annotation { "Feature Type Name" : "Feature", "Feature Type Description" : "" }
export const myFeature = defineFeature(function(context is Context, id is Id, definition is map)
    precondition{}
    {
        {
            var Q0;
            Q0=qCreatedBy(makeId("Top.planeOp"),FACE);
            var sketch = newSketch(context, id + "F0", { "sketchPlane" : qUnion([Q0])});
            skLineSegment(sketch, "E0.top", {"start": v(0, -101.6) * mm, "end": v(203.2, -101.6) * mm});
            skLineSegment(sketch, "E0.left", {"start": v(0, 0) * mm, "end": v(0, -101.6) * mm});
            skLineSegment(sketch, "E0.right", {"start": v(203.2, 0) * mm, "end": v(203.2, -101.6) * mm});
            skLineSegment(sketch, "E1.left", {"start": v(3.18, -3.17) * mm, "end": v(3.18, -98.43) * mm});
            skLineSegment(sketch, "E1.right", {"start": v(200.03, -3.17) * mm, "end": v(200.03, -98.43) * mm});
            skLineSegment(sketch, "E2", {"start": v(3.17, -3.17) * mm, "end": v(33.34, -3.17) * mm});
            skLineSegment(sketch, "E3", {"start": v(203.2, 0) * mm, "end": v(0, 0) * mm});
            skLineSegment(sketch, "E4", {"start": v(3.18, -98.43) * mm, "end": v(200.03, -98.43) * mm});
            skLineSegment(sketch, "E5.top", {"start": v(18.18, -98.43) * mm, "end": v(18.18, -98.43) * mm});
            skLineSegment(sketch, "E6", {"start": v(33.34, -98.43) * mm, "end": v(33.34, -3.17) * mm});
            skLineSegment(sketch, "E7", {"start": v(36.51, -3.17) * mm, "end": v(36.51, -3.17) * mm});
            skLineSegment(sketch, "E8", {"start": v(36.51, -3.17) * mm, "end": v(36.51, -98.43) * mm});
            skLineSegment(sketch, "E9", {"start": v(36.51, -3.17) * mm, "end": v(66.68, -3.17) * mm});
            skLineSegment(sketch, "E10", {"start": v(66.68, -98.42) * mm, "end": v(66.68, -3.17) * mm});
            skLineSegment(sketch, "E11", {"start": v(69.85, -3.17) * mm, "end": v(69.85, -98.42) * mm});
            skLineSegment(sketch, "E12", {"start": v(69.85, -3.17) * mm, "end": v(100.01, -3.17) * mm});
            skLineSegment(sketch, "E13", {"start": v(100.01, -3.17) * mm, "end": v(100.01, -98.42) * mm});
            skLineSegment(sketch, "E14", {"start": v(103.19, -3.17) * mm, "end": v(103.19, -98.42) * mm});
            skLineSegment(sketch, "E15", {"start": v(117.07, -3.17) * mm, "end": v(133.35, -3.17) * mm});
            skLineSegment(sketch, "E16", {"start": v(133.35, -3.17) * mm, "end": v(133.35, -98.42) * mm});
            skLineSegment(sketch, "E17", {"start": v(103.19, -3.17) * mm, "end": v(117.07, -3.17) * mm});
            skLineSegment(sketch, "E18", {"start": v(136.52, -3.17) * mm, "end": v(136.53, -98.42) * mm});
            skLineSegment(sketch, "E19", {"start": v(133.35, -3.17) * mm, "end": v(133.35, -3.17) * mm});
            skLineSegment(sketch, "E20", {"start": v(136.52, -3.17) * mm, "end": v(166.69, -3.17) * mm});
            skLineSegment(sketch, "E21", {"start": v(166.69, -3.17) * mm, "end": v(166.69, -98.42) * mm});
            skLineSegment(sketch, "E22", {"start": v(169.86, -3.17) * mm, "end": v(169.86, -98.42) * mm});
            skLineSegment(sketch, "E23", {"start": v(169.86, -3.17) * mm, "end": v(200.03, -3.17) * mm});
            skSolve(sketch);
        }
        {
            var Q0;
            Q0=makeQuery(id+"F0.imprint","IMPRINT",FACE,{"disambiguationData":[TD([[makeQuery(id+"F0.imprint","IMPRINT",EDGE,{"derivedFrom":sQuery(id+"F0.wireOp",EDGE,"E0.top")}),1.0]])]});
            var Q1;
            Q1=makeQuery(id+"F0.imprint","IMPRINT",FACE,{"disambiguationData":[TD([[makeQuery(id+"F0.imprint","IMPRINT",EDGE,{"derivedFrom":sQuery(id+"F0.wireOp",EDGE,"E5.bottom")}),-1.0]])]});
            var Q2;
            {var subQ0=sQuery(id+"F0.wireOp",EDGE,"646c8ae3-f2b2-429d-8022-bc64b3b6f105.1.0.0");Q2=makeQuery(id+"F0.imprint","IMPRINT",FACE,{"disambiguationData":[TD([[makeQuery(id+"F0.imprint","IMPRINT",EDGE,{"derivedFrom":subQ0}),1.0]])]});}
            var Q3;
            {var subQ0=sQuery(id+"F0.wireOp",EDGE,"646c8ae3-f2b2-429d-8022-bc64b3b6f105.2.0.0");Q3=makeQuery(id+"F0.imprint","IMPRINT",FACE,{"disambiguationData":[TD([[makeQuery(id+"F0.imprint","IMPRINT",EDGE,{"derivedFrom":subQ0}),1.0]])]});}
            var Q4;
            {var subQ0=sQuery(id+"F0.wireOp",EDGE,"646c8ae3-f2b2-429d-8022-bc64b3b6f105.3.0.0");Q4=makeQuery(id+"F0.imprint","IMPRINT",FACE,{"disambiguationData":[TD([[makeQuery(id+"F0.imprint","IMPRINT",EDGE,{"derivedFrom":subQ0}),1.0]])]});}
            var Q5;
            {var subQ0=sQuery(id+"F0.wireOp",EDGE,"646c8ae3-f2b2-429d-8022-bc64b3b6f105.4.0.0");Q5=makeQuery(id+"F0.imprint","IMPRINT",FACE,{"disambiguationData":[TD([[makeQuery(id+"F0.imprint","IMPRINT",EDGE,{"derivedFrom":subQ0}),1.0]])]});}
            var Q6;
            {var subQ0=sQuery(id+"F0.wireOp",EDGE,"646c8ae3-f2b2-429d-8022-bc64b3b6f105.5.0.0");Q6=makeQuery(id+"F0.imprint","IMPRINT",FACE,{"disambiguationData":[TD([[makeQuery(id+"F0.imprint","IMPRINT",EDGE,{"derivedFrom":subQ0}),1.0]])]});}
            var Q7;
            {var subQ0=sQuery(id+"F0.wireOp",EDGE,"646c8ae3-f2b2-429d-8022-bc64b3b6f105.6.0.0");Q7=makeQuery(id+"F0.imprint","IMPRINT",FACE,{"disambiguationData":[TD([[makeQuery(id+"F0.imprint","IMPRINT",EDGE,{"derivedFrom":subQ0}),1.0]])]});}
            var Q8;
            {var subQ0=sQuery(id+"F0.wireOp",EDGE,"646c8ae3-f2b2-429d-8022-bc64b3b6f105.7.0.0");Q8=makeQuery(id+"F0.imprint","IMPRINT",FACE,{"disambiguationData":[TD([[makeQuery(id+"F0.imprint","IMPRINT",EDGE,{"derivedFrom":subQ0}),1.0]])]});}
            var Q9;
            {var subQ0=sQuery(id+"F0.wireOp",EDGE,"646c8ae3-f2b2-429d-8022-bc64b3b6f105.8.0.0");Q9=makeQuery(id+"F0.imprint","IMPRINT",FACE,{"disambiguationData":[TD([[makeQuery(id+"F0.imprint","IMPRINT",EDGE,{"derivedFrom":subQ0}),1.0]])]});}
            var Q10;
            {var subQ0=sQuery(id+"F0.wireOp",EDGE,"646c8ae3-f2b2-429d-8022-bc64b3b6f105.9.0.0");Q10=makeQuery(id+"F0.imprint","IMPRINT",FACE,{"disambiguationData":[TD([[makeQuery(id+"F0.imprint","IMPRINT",EDGE,{"derivedFrom":subQ0}),1.0]])]});}
            extrude(context, id + "F1", {"entities" : qUnion([Q0, Q1, Q2, Q3, Q4, Q5, Q6, Q7, Q8, Q9, Q10]), "depth" : 47.62 * mm, "offsetDistance" : 25.4 * mm});
        }
        {
            var Q0;
            Q0=makeQuery(id+"FWKmPxKbktaoT75_1.boolean.opBoolean","MERGE",FACE,{"derivedFrom":[makeQuery(id+"F1.opExtrude","SWEPT_FACE",FACE,{"disambiguationData":[OSD([sQuery(id+"F0.wireOp",EDGE,"E0.top")])]}),makeQuery(id+"FWKmPxKbktaoT75_1.opExtrude","SWEPT_FACE",FACE,{"disambiguationData":[OSD([sQuery(id+"FPa2vzEjn9xWxvl_1.wireOp",EDGE,"pVME8pcI-fUVT-DpI0-aKQs-MaaHCtd98V99.bottom")])]})]});
            var sketch = newSketch(context, id + "F2", { "sketchPlane" : qUnion([Q0])});
            skText(sketch, "E24", { "text": "Black Heat Shrink", "fontName": "OpenSans-Regular.ttf"});
            const initialGuessF2  = {"E24": [0.00394, 0.01524, 1, 0, 0.01715]};
            skSetInitialGuess(sketch, initialGuessF2);
            skSolve(sketch);
        }
        {
            var Q0;
            Q0=qSketchRegion(id+"F2",true);
            extrude(context, id + "F3", {"entities" : qUnion([Q0]), "operationType" : NewBodyOperationType.REMOVE, "oppositeDirection" : true, "depth" : 0.25 * mm, "offsetDistance" : 25.4 * mm});
        }
        {
            var Q0;
            Q0=makeQuery(id+"F1.opExtrude","CAP_FACE",FACE,{"disambiguationData":[OSD([sQuery(id+"F0.wireOp",EDGE,"E0.top"),sQuery(id+"F0.wireOp",EDGE,"E0.left"),sQuery(id+"F0.wireOp",EDGE,"E0.right"),sQuery(id+"F0.wireOp",EDGE,"E1.left"),sQuery(id+"F0.wireOp",EDGE,"E1.right"),sQuery(id+"F0.wireOp",EDGE,"E2"),sQuery(id+"F0.wireOp",EDGE,"E3"),sQuery(id+"F0.wireOp",EDGE,"E4"),sQuery(id+"F0.wireOp",EDGE,"E6"),sQuery(id+"F0.wireOp",EDGE,"E8"),sQuery(id+"F0.wireOp",EDGE,"E9"),sQuery(id+"F0.wireOp",EDGE,"E10"),sQuery(id+"F0.wireOp",EDGE,"E11"),sQuery(id+"F0.wireOp",EDGE,"E12"),sQuery(id+"F0.wireOp",EDGE,"E13"),sQuery(id+"F0.wireOp",EDGE,"E14"),sQuery(id+"F0.wireOp",EDGE,"E15"),sQuery(id+"F0.wireOp",EDGE,"E16"),sQuery(id+"F0.wireOp",EDGE,"E17"),sQuery(id+"F0.wireOp",EDGE,"E18"),sQuery(id+"F0.wireOp",EDGE,"E20"),sQuery(id+"F0.wireOp",EDGE,"E21"),sQuery(id+"F0.wireOp",EDGE,"E22"),sQuery(id+"F0.wireOp",EDGE,"E23")])],"isStart":true});
            var sketch = newSketch(context, id + "F4", { "sketchPlane" : qUnion([Q0])});
            skLineSegment(sketch, "E25.bottom", {"start": v(0, 101.6) * mm, "end": v(203.2, 101.6) * mm});
            skLineSegment(sketch, "E25.top", {"start": v(0, 0) * mm, "end": v(203.2, 0) * mm});
            skLineSegment(sketch, "E25.left", {"start": v(0, 101.6) * mm, "end": v(0, 0) * mm});
            skLineSegment(sketch, "E25.right", {"start": v(203.2, 101.6) * mm, "end": v(203.2, 0) * mm});
            skSolve(sketch);
        }
        {
            var Q0;
            Q0 = qSketchRegion(id + "F4", true);
            extrude(context, id + "F5", {"entities" : qUnion([Q0]), "operationType" : NewBodyOperationType.ADD, "depth" : 3.17 * mm, "offsetDistance" : 25.4 * mm});
        }
    });